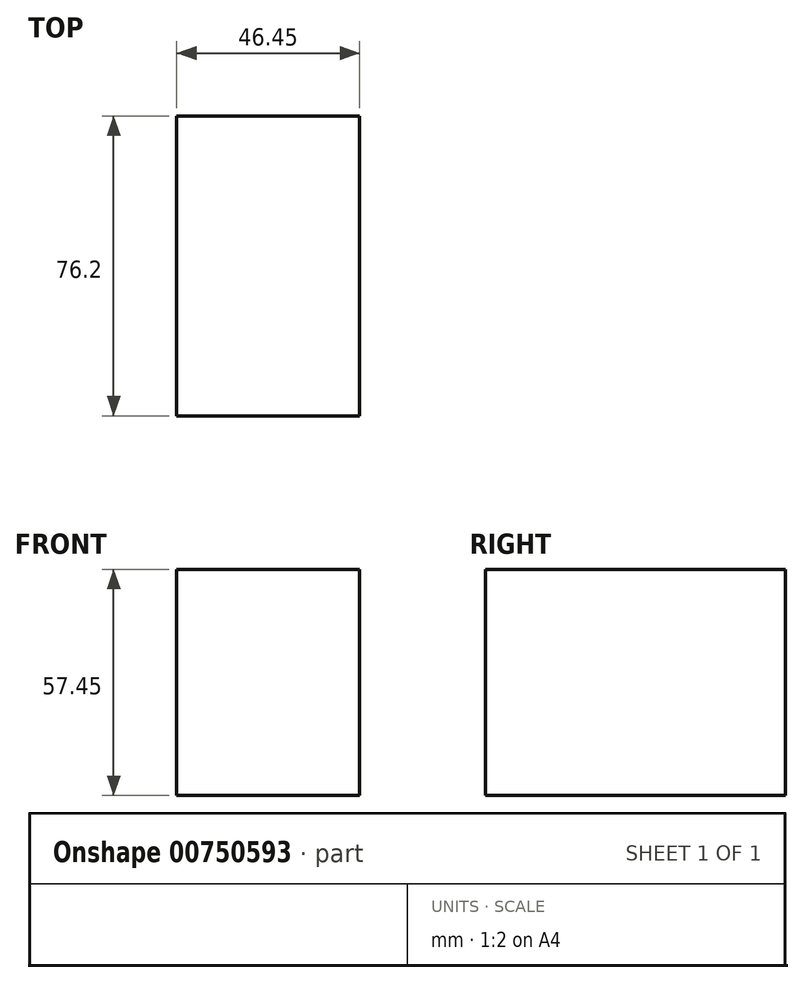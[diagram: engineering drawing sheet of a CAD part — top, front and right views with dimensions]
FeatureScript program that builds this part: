
annotation { "Feature Type Name" : "Feature", "Feature Type Description" : "" }
export const myFeature = defineFeature(function(context is Context, id is Id, definition is map)
    precondition{}
    {
        {
            var Q0;
            Q0=qCreatedBy(makeId("Front.planeOp"),FACE);
            var sketch = newSketch(context, id + "F0", { "sketchPlane" : qUnion([Q0])});
            skLineSegment(sketch, "E0.bottom", {"start": v(-23.6, 25.88) * mm, "end": v(22.85, 25.88) * mm});
            skLineSegment(sketch, "E0.top", {"start": v(-23.6, -31.57) * mm, "end": v(22.85, -31.57) * mm});
            skLineSegment(sketch, "E0.left", {"start": v(-23.6, 25.88) * mm, "end": v(-23.6, -31.57) * mm});
            skLineSegment(sketch, "E0.right", {"start": v(22.85, 25.88) * mm, "end": v(22.85, -31.57) * mm});
            skSolve(sketch);
        }
        {
            var Q0;
            Q0=makeQuery(id+"F0.imprint","IMPRINT",FACE,{"disambiguationData":[TD([[makeQuery(id+"F0.imprint","IMPRINT",EDGE,{"derivedFrom":sQuery(id+"F0.wireOp",EDGE,"E0.bottom")}),-1.0]])]});
            extrude(context, id + "F1", {"entities" : qUnion([Q0]), "oppositeDirection" : true, "depth" : 76.2 * mm, "offsetDistance" : 25.4 * mm});
        }
    });
